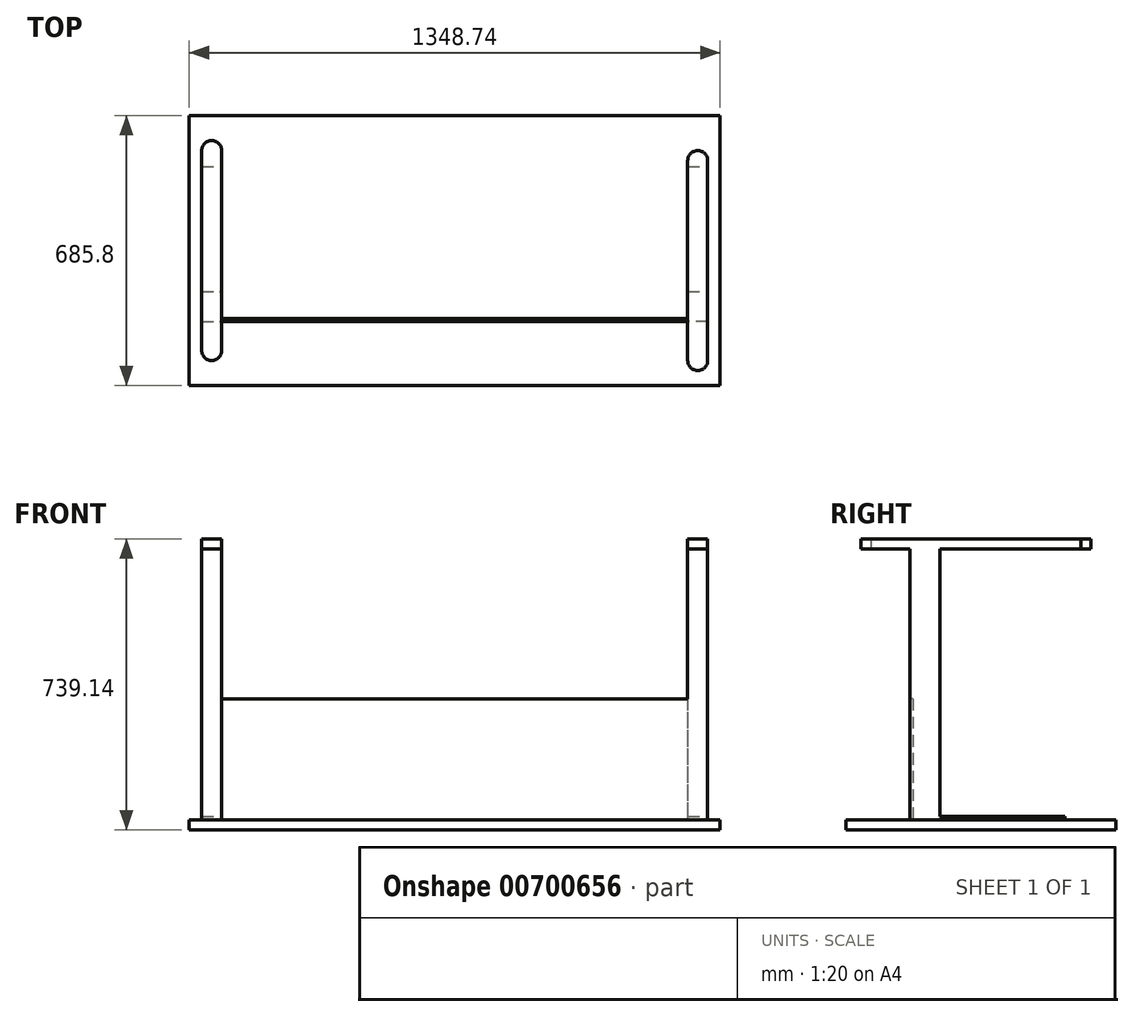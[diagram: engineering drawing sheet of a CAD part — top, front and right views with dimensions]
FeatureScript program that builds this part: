
annotation { "Feature Type Name" : "Feature", "Feature Type Description" : "" }
export const myFeature = defineFeature(function(context is Context, id is Id, definition is map)
    precondition{}
    {
        {
            var Q0;
            Q0=qCreatedBy(makeId("Top.planeOp"),FACE);
            var sketch = newSketch(context, id + "F0", { "sketchPlane" : qUnion([Q0])});
            skLineSegment(sketch, "E0.bottom", {"start": v(-658.53, 409.58) * mm, "end": v(690.2, 409.58) * mm});
            skLineSegment(sketch, "E0.top", {"start": v(-658.53, -276.22) * mm, "end": v(690.2, -276.22) * mm});
            skLineSegment(sketch, "E0.left", {"start": v(-658.53, 409.58) * mm, "end": v(-658.53, -276.22) * mm});
            skLineSegment(sketch, "E0.right", {"start": v(690.2, 409.58) * mm, "end": v(690.2, -276.22) * mm});
            skSolve(sketch);
        }
        {
            var Q0;
            Q0 = qSketchRegion(id + "F0", true);
            extrude(context, id + "F1", {"entities" : qUnion([Q0]), "oppositeDirection" : true, "depth" : 25.4 * mm, "offsetDistance" : 25.4 * mm});
        }
        {
            var Q0;
            Q0=makeQuery(id+"F1.opExtrude","CAP_FACE",FACE,{"disambiguationData":[OSD([sQuery(id+"F0.wireOp",EDGE,"E0.bottom"),sQuery(id+"F0.wireOp",EDGE,"E0.top"),sQuery(id+"F0.wireOp",EDGE,"E0.left"),sQuery(id+"F0.wireOp",EDGE,"E0.right")])],"isStart":true});
            var sketch = newSketch(context, id + "F2", { "sketchPlane" : qUnion([Q0])});
            skSolve(sketch);
        }
        {
            var Q0;
            Q0=makeQuery(id+"F2.imprint","IMPRINT",FACE,{"disambiguationData":[TD([[makeQuery(id+"F2.imprint","IMPRINT",EDGE,{"derivedFrom":makeQuery(id+"F1.opExtrude","CAP_EDGE",EDGE,{"disambiguationData":[OSD([sQuery(id+"F0.wireOp",EDGE,"E0.bottom")])],"isStart":true})}),-1.0]])]});
            var sketch = newSketch(context, id + "F3", { "sketchPlane" : qUnion([Q0])});
            skSolve(sketch);
        }
        {
            var Q0;
            Q0=makeQuery(id+"F3.imprint","IMPRINT",FACE,{"disambiguationData":[TD([[makeQuery(id+"F3.imprint","IMPRINT",EDGE,{"derivedFrom":makeQuery(id+"F2.imprint","IMPRINT",EDGE,{"derivedFrom":makeQuery(id+"F1.opExtrude","CAP_EDGE",EDGE,{"disambiguationData":[OSD([sQuery(id+"F0.wireOp",EDGE,"E0.bottom")])],"isStart":true})})}),-1.0]])]});
            var sketch = newSketch(context, id + "F4", { "sketchPlane" : qUnion([Q0])});
            skLineSegment(sketch, "E1.bottom", {"start": v(-626.78, 279.4) * mm, "end": v(-575.98, 279.4) * mm});
            skLineSegment(sketch, "E1.top", {"start": v(-626.78, -38.1) * mm, "end": v(-575.98, -38.1) * mm});
            skLineSegment(sketch, "E1.left", {"start": v(-626.78, 279.4) * mm, "end": v(-626.78, -38.1) * mm});
            skLineSegment(sketch, "E1.right", {"start": v(-575.98, 279.4) * mm, "end": v(-575.98, -38.1) * mm});
            skLineSegment(sketch, "E2.bottom", {"start": v(607.66, 279.4) * mm, "end": v(658.46, 279.4) * mm});
            skLineSegment(sketch, "E2.top", {"start": v(607.66, -38.1) * mm, "end": v(658.46, -38.1) * mm});
            skLineSegment(sketch, "E2.left", {"start": v(607.66, 279.4) * mm, "end": v(607.66, -38.1) * mm});
            skLineSegment(sketch, "E2.right", {"start": v(658.46, 279.4) * mm, "end": v(658.46, -38.1) * mm});
            skSolve(sketch);
        }
        {
            var Q0;
            Q0 = qSketchRegion(id + "F4", true);
            extrude(context, id + "F5", {"entities" : qUnion([Q0]), "operationType" : NewBodyOperationType.ADD, "depth" : 9.52 * mm, "offsetDistance" : 25.4 * mm});
        }
        {
            var Q0;
            Q0=makeQuery(id+"F1.opExtrude","CAP_FACE",FACE,{"disambiguationData":[OSD([sQuery(id+"F0.wireOp",EDGE,"E0.bottom"),sQuery(id+"F0.wireOp",EDGE,"E0.top"),sQuery(id+"F0.wireOp",EDGE,"E0.left"),sQuery(id+"F0.wireOp",EDGE,"E0.right")])],"isStart":true});
            var sketch = newSketch(context, id + "F6", { "sketchPlane" : qUnion([Q0])});
            skLineSegment(sketch, "E3.bottom", {"start": v(-620.43, 279.4) * mm, "end": v(-575.98, 279.4) * mm});
            skLineSegment(sketch, "E3.top", {"start": v(-620.43, -177.8) * mm, "end": v(-575.98, -177.8) * mm});
            skLineSegment(sketch, "E3.left", {"start": v(-620.43, 279.4) * mm, "end": v(-620.43, -177.8) * mm});
            skLineSegment(sketch, "E3.right", {"start": v(-575.98, 279.4) * mm, "end": v(-575.98, -177.8) * mm});
            skLineSegment(sketch, "E4.bottom", {"start": v(607.66, 139.7) * mm, "end": v(652.1, 139.7) * mm});
            skLineSegment(sketch, "E4.top", {"start": v(607.66, -177.8) * mm, "end": v(652.1, -177.8) * mm});
            skLineSegment(sketch, "E4.left", {"start": v(607.66, 139.7) * mm, "end": v(607.66, -177.8) * mm});
            skLineSegment(sketch, "E4.right", {"start": v(652.1, 139.7) * mm, "end": v(652.1, -177.8) * mm});
            skSolve(sketch);
        }
        {
            var Q0;
            Q0=makeQuery(id+"F2.imprint","IMPRINT",FACE,{"disambiguationData":[TD([[makeQuery(id+"F2.imprint","IMPRINT",EDGE,{"derivedFrom":makeQuery(id+"F1.opExtrude","CAP_EDGE",EDGE,{"disambiguationData":[OSD([sQuery(id+"F0.wireOp",EDGE,"E0.bottom")])],"isStart":true})}),-1.0]])]});
            var sketch = newSketch(context, id + "F7", { "sketchPlane" : qUnion([Q0])});
            skLineSegment(sketch, "E5.bottom", {"start": v(-627.11, -38.1) * mm, "end": v(-576.31, -38.1) * mm});
            skLineSegment(sketch, "E5.top", {"start": v(-627.11, -114.3) * mm, "end": v(-576.31, -114.3) * mm});
            skLineSegment(sketch, "E5.left", {"start": v(-627.11, -38.1) * mm, "end": v(-627.11, -114.3) * mm});
            skLineSegment(sketch, "E5.right", {"start": v(-576.31, -38.1) * mm, "end": v(-576.31, -114.3) * mm});
            skLineSegment(sketch, "E6.bottom", {"start": v(658.46, -38.1) * mm, "end": v(607.66, -38.1) * mm});
            skLineSegment(sketch, "E6.top", {"start": v(658.46, -114.3) * mm, "end": v(607.66, -114.3) * mm});
            skLineSegment(sketch, "E6.left", {"start": v(658.46, -38.1) * mm, "end": v(658.46, -114.3) * mm});
            skLineSegment(sketch, "E6.right", {"start": v(607.66, -38.1) * mm, "end": v(607.66, -114.3) * mm});
            skSolve(sketch);
        }
        {
            var Q0;
            Q0 = qSketchRegion(id + "F7", true);
            extrude(context, id + "F8", {"entities" : qUnion([Q0]), "operationType" : NewBodyOperationType.ADD, "depth" : 688.34 * mm, "offsetDistance" : 25.4 * mm});
        }
        {
            var Q0;
            Q0=makeQuery(id+"F8.opExtrude","CAP_FACE",FACE,{"disambiguationData":[OSD([sQuery(id+"F7.wireOp",EDGE,"E5.bottom"),sQuery(id+"F7.wireOp",EDGE,"E5.top"),sQuery(id+"F7.wireOp",EDGE,"E5.left"),sQuery(id+"F7.wireOp",EDGE,"E5.right")])],"isStart":false});
            var sketch = newSketch(context, id + "F9", { "sketchPlane" : qUnion([Q0])});
            skLineSegment(sketch, "E7", {"start": v(-601.71, -212.72) * mm, "end": v(-601.71, -212.72) * mm});
            skLineSegment(sketch, "E8", {"start": v(-576.31, -187.32) * mm, "end": v(-576.31, 320.68) * mm});
            skLineSegment(sketch, "E9", {"start": v(-601.71, 346.08) * mm, "end": v(-601.71, 346.08) * mm});
            skLineSegment(sketch, "E10", {"start": v(-627.11, 320.68) * mm, "end": v(-627.11, -187.32) * mm});
            skPoint(sketch, "E11.visualSharp", {"position": v(-627.11, 346.08) * mm});
            skArc(sketch, "E11.filletArc", {"start": v(-601.71, 346.08) * mm, "mid": v(-619.67, 338.64) * mm, "end": v(-627.11, 320.68) * mm});
            skPoint(sketch, "E12.visualSharp", {"position": v(-576.31, 346.08) * mm});
            skArc(sketch, "E12.filletArc", {"start": v(-576.31, 320.68) * mm, "mid": v(-583.75, 338.64) * mm, "end": v(-601.71, 346.08) * mm});
            skPoint(sketch, "E13.visualSharp", {"position": v(-576.31, -114.3) * mm});
            skArc(sketch, "E13.filletArc", {"start": v(-601.71, -212.72) * mm, "mid": v(-583.75, -205.28) * mm, "end": v(-576.31, -187.32) * mm});
            skPoint(sketch, "E14.visualSharp", {"position": v(-627.11, -114.3) * mm});
            skArc(sketch, "E14.filletArc", {"start": v(-627.11, -187.32) * mm, "mid": v(-619.67, -205.28) * mm, "end": v(-601.71, -212.72) * mm});
            skSolve(sketch);
        }
        {
            var Q0;
            Q0 = qSketchRegion(id + "F9", true);
            extrude(context, id + "F10", {"entities" : qUnion([Q0]), "operationType" : NewBodyOperationType.ADD, "depth" : 25.4 * mm, "offsetDistance" : 25.4 * mm});
        }
        {
            var Q0;
            Q0=makeQuery(id+"F8.opExtrude","CAP_FACE",FACE,{"disambiguationData":[OSD([sQuery(id+"F7.wireOp",EDGE,"E6.bottom"),sQuery(id+"F7.wireOp",EDGE,"E6.top"),sQuery(id+"F7.wireOp",EDGE,"E6.left"),sQuery(id+"F7.wireOp",EDGE,"E6.right")])],"isStart":false});
            var sketch = newSketch(context, id + "F11", { "sketchPlane" : qUnion([Q0])});
            skLineSegment(sketch, "E15", {"start": v(658.46, -263.52) * mm, "end": v(658.46, -212.72) * mm});
            skLineSegment(sketch, "E16", {"start": v(658.46, -263.52) * mm, "end": v(658.46, 295.28) * mm});
            skLineSegment(sketch, "E17", {"start": v(633.06, 320.68) * mm, "end": v(633.06, 320.68) * mm});
            skLineSegment(sketch, "E18", {"start": v(607.66, 295.28) * mm, "end": v(607.66, -212.72) * mm});
            skPoint(sketch, "E19.visualSharp", {"position": v(607.66, 320.68) * mm});
            skArc(sketch, "E19.filletArc", {"start": v(633.06, 320.68) * mm, "mid": v(615.1, 313.24) * mm, "end": v(607.66, 295.28) * mm});
            skPoint(sketch, "E20.visualSharp", {"position": v(658.46, 320.68) * mm});
            skArc(sketch, "E20.filletArc", {"start": v(658.46, 295.28) * mm, "mid": v(651.02, 313.24) * mm, "end": v(633.06, 320.68) * mm});
            skPoint(sketch, "E21.visualSharp", {"position": v(607.66, -114.3) * mm});
            skArc(sketch, "E21.filletArc", {"start": v(607.66, -212.72) * mm, "mid": v(633.06, -238.12) * mm, "end": v(658.46, -212.72) * mm});
            skPoint(sketch, "E22.visualSharp", {"position": v(658.46, -114.3) * mm});
            skLineSegment(sketch, "E22.filletArc", {"start": v(658.46, -263.52) * mm, "end": v(658.46, -263.52) * mm});
            skSolve(sketch);
        }
        {
            var Q0;
            Q0 = qSketchRegion(id + "F11", true);
            extrude(context, id + "F12", {"entities" : qUnion([Q0]), "operationType" : NewBodyOperationType.ADD, "depth" : 25.4 * mm, "offsetDistance" : 25.4 * mm});
        }
        {
            var Q0;
            {var subQ12=sQuery(id+"F6.wireOp",EDGE,"E3.bottom");Q0=makeQuery(id+"F6.imprint","IMPRINT",FACE,{"disambiguationData":[TD([[makeQuery(id+"F6.imprint","IMPRINT",EDGE,{"derivedFrom":subQ12}),1.0]])]});}
            var sketch = newSketch(context, id + "F13", { "sketchPlane" : qUnion([Q0])});
            skLineSegment(sketch, "E23", {"start": v(-575.98, -114.3) * mm, "end": v(607.66, -114.3) * mm});
            skLineSegment(sketch, "E24", {"start": v(607.66, -114.3) * mm, "end": v(607.66, -106.04) * mm});
            skLineSegment(sketch, "E25", {"start": v(607.66, -106.04) * mm, "end": v(-575.98, -106.04) * mm});
            skLineSegment(sketch, "E26", {"start": v(-575.98, -106.04) * mm, "end": v(-575.98, -114.3) * mm});
            skSolve(sketch);
        }
        {
            var Q0;
            Q0=makeQuery(id+"F13.imprint","IMPRINT",FACE,{"disambiguationData":[TD([[makeQuery(id+"F13.imprint","IMPRINT",EDGE,{"derivedFrom":sQuery(id+"F13.wireOp",EDGE,"E23")}),1.0]])]});
            extrude(context, id + "F14", {"entities" : qUnion([Q0]), "operationType" : NewBodyOperationType.ADD, "depth" : 307.97 * mm, "offsetDistance" : 25.4 * mm});
        }
    });
